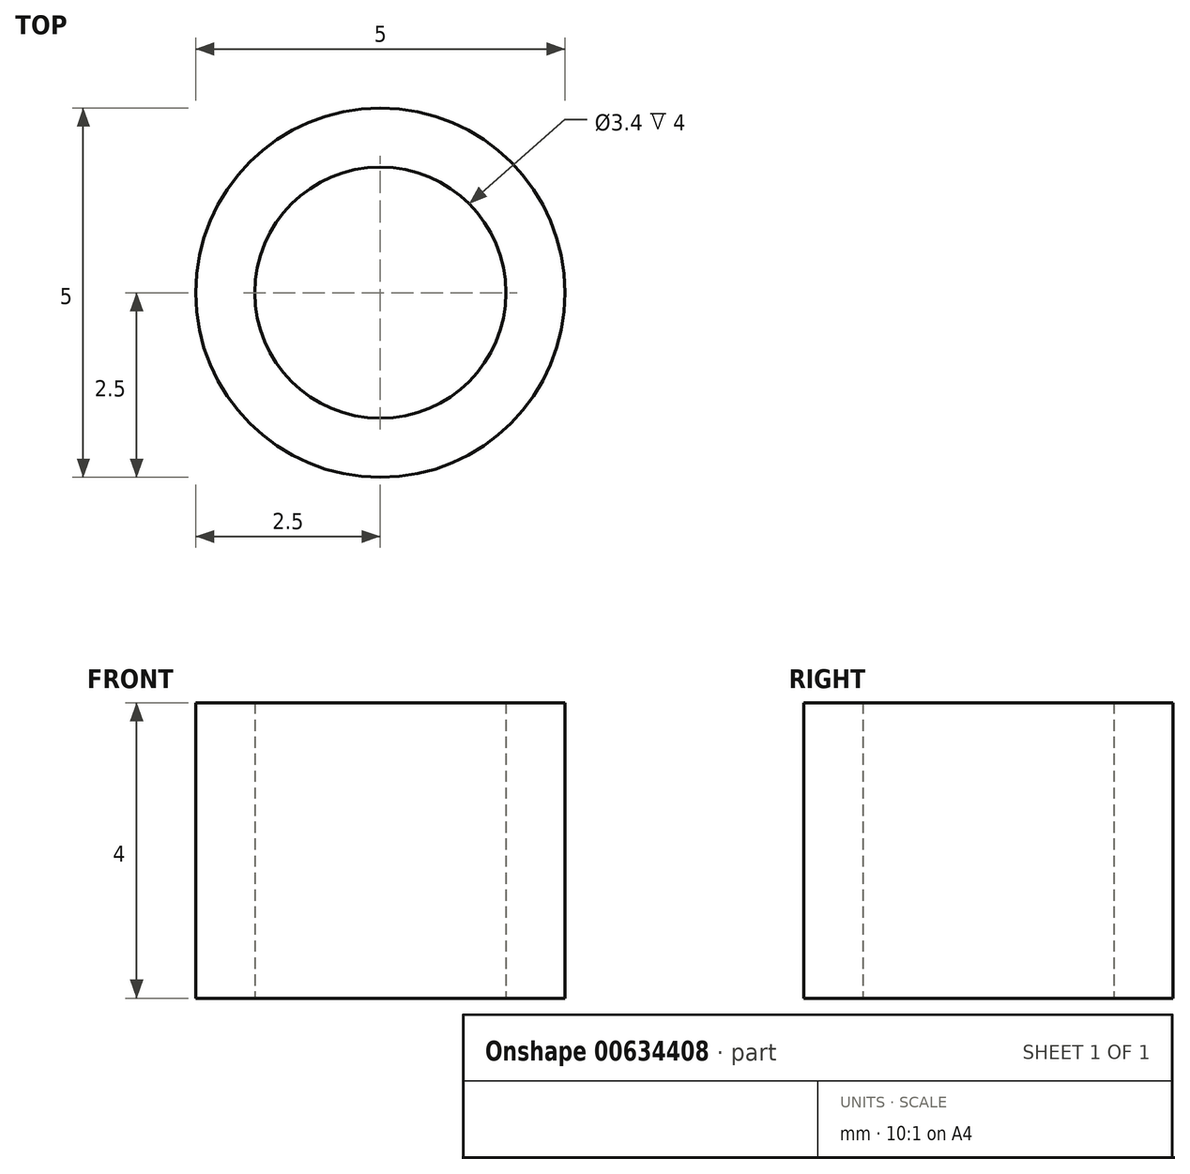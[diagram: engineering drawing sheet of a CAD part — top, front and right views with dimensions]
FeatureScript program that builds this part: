
annotation { "Feature Type Name" : "Feature", "Feature Type Description" : "" }
export const myFeature = defineFeature(function(context is Context, id is Id, definition is map)
    precondition{}
    {
        {
            var Q0;
            Q0=qCreatedBy(makeId("Top.planeOp"),FACE);
            var sketch = newSketch(context, id + "F0", { "sketchPlane" : qUnion([Q0])});
            skCircle(sketch, "E0", {"center": v(0, 0) * mm, "radius": 1.7 * mm});
            skCircle(sketch, "E1", {"center": v(0, 0) * mm, "radius": 2.5 * mm});
            skSolve(sketch);
        }
        {
            var Q0;
            Q0 = qSketchRegion(id + "F0", true);
            extrude(context, id + "F1", {"entities" : qUnion([Q0]), "depth" : 4 * mm, "offsetDistance" : 25 * mm});
        }
    });
